FCSTD DOCUMENT  (FreeCAD 0.19R0.19.2)
Label: 002
License: All rights reserved
LicenseURL: http://en.wikipedia.org/wiki/All_rights_reserved
objects: Sketcher::SketchObject×1
note: 1 computed .brp shape members not serialized (recipe doc carries the construction recipe); baked Part::Feature solids carry a one-line shape summary decoded from their .brp

FEATURE [Sketcher::SketchObject] Sketch
  FullyConstrained = false
  sketch-geometry (17):
    g0: Circle CenterX=-16.25 CenterY=0 CenterZ=0 NormalX=0 NormalY=0 NormalZ=1 AngleXU=0 Radius=1.5
    g1: Circle CenterX=16.25 CenterY=0 CenterZ=0 NormalX=0 NormalY=0 NormalZ=1 AngleXU=0 Radius=1.5
    g2: LineSegment StartX=21.05 StartY=0 StartZ=0 EndX=21.05 EndY=-1 EndZ=0
    g3: LineSegment StartX=21.05 StartY=-1 StartZ=0 EndX=10.05 EndY=-1 EndZ=0
    g4: LineSegment StartX=21.05 StartY=-1 StartZ=0 EndX=21.05 EndY=-4.3 EndZ=0
    g5: LineSegment StartX=16.25 StartY=-4.3 StartZ=0 EndX=21.05 EndY=-4.3 EndZ=0
    g6: LineSegment StartX=16.25 StartY=-4.3 StartZ=0 EndX=13.65 EndY=-4.3 EndZ=0
    g7: LineSegment StartX=-21.05 StartY=0 StartZ=0 EndX=-21.05 EndY=-1 EndZ=0
    g8: LineSegment StartX=-10.05 StartY=-1 StartZ=0 EndX=-21.05 EndY=-1 EndZ=0
    g9: LineSegment StartX=-21.05 StartY=-1 StartZ=0 EndX=-21.05 EndY=-4.3 EndZ=0
    g10: LineSegment StartX=-21.05 StartY=-4.3 StartZ=0 EndX=-16.25 EndY=-4.3 EndZ=0
    g11: LineSegment StartX=-13.65 StartY=-4.3 StartZ=0 EndX=-16.25 EndY=-4.3 EndZ=0
    g12: LineSegment StartX=-16.25 StartY=4.3 StartZ=0 EndX=21.05 EndY=4.3 EndZ=0
    g13: LineSegment StartX=-16.25 StartY=4.3 StartZ=0 EndX=-21.05 EndY=4.3 EndZ=0
    g14: LineSegment StartX=-21.05 StartY=0 StartZ=0 EndX=-21.05 EndY=4.3 EndZ=0
    g15: LineSegment StartX=21.05 StartY=0 StartZ=0 EndX=21.05 EndY=4.3 EndZ=0
    g16: LineSegment StartX=-10.1373 StartY=-3.96711 StartZ=0 EndX=-11.7373 EndY=-3.96711 EndZ=0
  constraints (42):
    c: Block(g1)
    c: Block(g0)
    c: Vertical(g2)
    c: Horizontal(g3)
    c: Coincident(g3,g2)
    c: Coincident(g4,g2)
    c: Vertical(g4)
    c: Block(g2)
    c: Block(g3)
    c: Horizontal(g5)
    c: Coincident(g5,g4)
    c: Horizontal(g6)
    c: Distance(g6) = 2.6
    c: Vertical(g7)
    c: Block(g7)
    c: Horizontal(g8)
    c: Coincident(g8,g7)
    c: Distance(g3) = 11
    c: Distance(g8) = 11
    c: Vertical(g9)
    c: Coincident(g9,g7)
    c: Distance(g9) = 3.3
    c: Horizontal(g10)
    c: Coincident(g10,g9)
    c: Distance(g10) = 4.8
    c: Horizontal(g11)
    c: Equal(g6,g11) = 2.6
    c: Coincident(g11,g10)
    c: Horizontal(g12)
    c: Horizontal(g13)
    c: Vertical(g14)
    c: Coincident(g14,g13)
    c: Vertical(g15)
    c: Coincident(g15,g12)
    c: Block(g12)
    c: Block(g14)
    c: Block(g13)
    c: Block(g15)
    c: Block(g5)
    c: Block(g6)
    c: Horizontal(g16)
    c: Distance(g16) = 1.6
